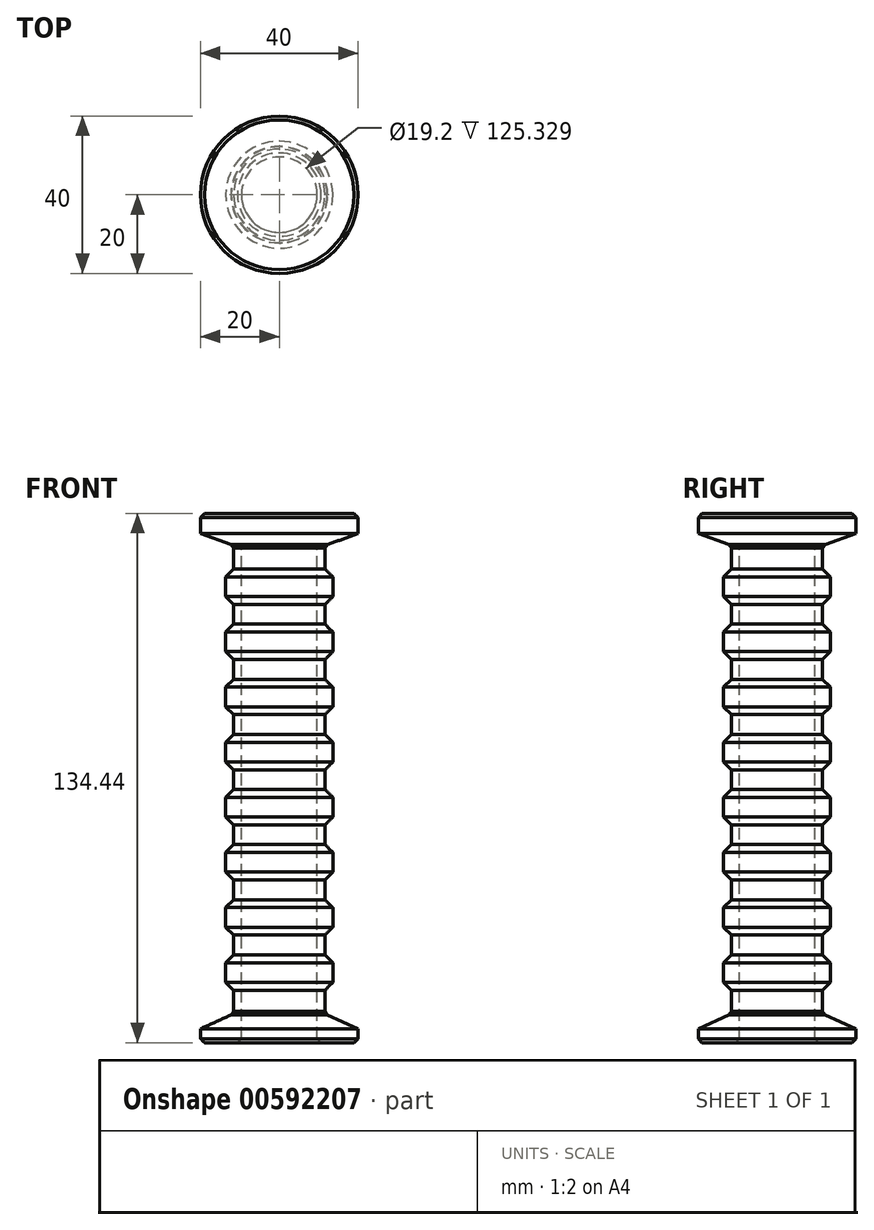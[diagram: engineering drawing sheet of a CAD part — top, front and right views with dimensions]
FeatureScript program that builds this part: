
annotation { "Feature Type Name" : "Feature", "Feature Type Description" : "" }
export const myFeature = defineFeature(function(context is Context, id is Id, definition is map)
    precondition{}
    {
        {
            var Q0;
            Q0=qCreatedBy(makeId("Front.planeOp"),FACE);
            var sketch = newSketch(context, id + "F0", { "sketchPlane" : qUnion([Q0])});
            skLineSegment(sketch, "E0", {"start": v(0, 89.56) * mm, "end": v(0, -84.94) * mm, "construction": true});
            skLineSegment(sketch, "E1", {"start": v(0, 55.8) * mm, "end": v(-20, 55.8) * mm});
            skLineSegment(sketch, "E2", {"start": v(-20, 55.8) * mm, "end": v(-20, 50.7) * mm});
            skLineSegment(sketch, "E3", {"start": v(-20, 50.7) * mm, "end": v(-11.6, 47.7) * mm});
            skLineSegment(sketch, "E4", {"start": v(-11.6, 47.7) * mm, "end": v(-11.6, 40.7) * mm, "construction": true});
            skLineSegment(sketch, "E5.bottom", {"start": v(-11.6, 40.7) * mm, "end": v(-13.6, 40.7) * mm});
            skLineSegment(sketch, "E5.top", {"start": v(-11.6, 33.7) * mm, "end": v(-13.6, 33.7) * mm});
            skLineSegment(sketch, "E5.right", {"start": v(-13.6, 40.7) * mm, "end": v(-13.6, 33.7) * mm});
            skLineSegment(sketch, "E6", {"start": v(-11.6, 47.7) * mm, "end": v(-11.6, 40.7) * mm});
            skLineSegment(sketch, "E7.0.1.0", {"start": v(-11.6, 33.7) * mm, "end": v(-11.6, 26.7) * mm});
            skLineSegment(sketch, "E7.0.1.1", {"start": v(-11.6, 26.7) * mm, "end": v(-13.6, 26.7) * mm});
            skLineSegment(sketch, "E7.0.1.2", {"start": v(-13.6, 26.7) * mm, "end": v(-13.6, 19.7) * mm});
            skLineSegment(sketch, "E7.0.1.3", {"start": v(-11.6, 19.7) * mm, "end": v(-13.6, 19.7) * mm});
            skLineSegment(sketch, "E7.0.2.0", {"start": v(-11.6, 19.7) * mm, "end": v(-11.6, 12.7) * mm});
            skLineSegment(sketch, "E7.0.2.1", {"start": v(-11.6, 12.7) * mm, "end": v(-13.6, 12.7) * mm});
            skLineSegment(sketch, "E7.0.2.2", {"start": v(-13.6, 12.7) * mm, "end": v(-13.6, 5.7) * mm});
            skLineSegment(sketch, "E7.0.2.3", {"start": v(-11.6, 5.7) * mm, "end": v(-13.6, 5.7) * mm});
            skLineSegment(sketch, "E7.0.3.0", {"start": v(-11.6, 5.7) * mm, "end": v(-11.6, -1.3) * mm});
            skLineSegment(sketch, "E7.0.3.1", {"start": v(-11.6, -1.3) * mm, "end": v(-13.6, -1.3) * mm});
            skLineSegment(sketch, "E7.0.3.2", {"start": v(-13.6, -1.3) * mm, "end": v(-13.6, -8.3) * mm});
            skLineSegment(sketch, "E7.0.3.3", {"start": v(-11.6, -8.3) * mm, "end": v(-13.6, -8.3) * mm});
            skLineSegment(sketch, "E7.0.4.0", {"start": v(-11.6, -8.3) * mm, "end": v(-11.6, -15.3) * mm});
            skLineSegment(sketch, "E7.0.4.1", {"start": v(-11.6, -15.3) * mm, "end": v(-13.6, -15.3) * mm});
            skLineSegment(sketch, "E7.0.4.2", {"start": v(-13.6, -15.3) * mm, "end": v(-13.6, -22.3) * mm});
            skLineSegment(sketch, "E7.0.4.3", {"start": v(-11.6, -22.3) * mm, "end": v(-13.6, -22.3) * mm});
            skLineSegment(sketch, "E7.0.5.0", {"start": v(-11.6, -22.3) * mm, "end": v(-11.6, -29.3) * mm});
            skLineSegment(sketch, "E7.0.5.1", {"start": v(-11.6, -29.3) * mm, "end": v(-13.6, -29.3) * mm});
            skLineSegment(sketch, "E7.0.5.2", {"start": v(-13.6, -29.3) * mm, "end": v(-13.6, -36.3) * mm});
            skLineSegment(sketch, "E7.0.5.3", {"start": v(-11.6, -36.3) * mm, "end": v(-13.6, -36.3) * mm});
            skLineSegment(sketch, "E7.0.6.0", {"start": v(-11.6, -36.3) * mm, "end": v(-11.6, -43.3) * mm});
            skLineSegment(sketch, "E7.0.6.1", {"start": v(-11.6, -43.3) * mm, "end": v(-13.6, -43.3) * mm});
            skLineSegment(sketch, "E7.0.6.2", {"start": v(-13.6, -43.3) * mm, "end": v(-13.6, -50.3) * mm});
            skLineSegment(sketch, "E7.0.6.3", {"start": v(-11.6, -50.3) * mm, "end": v(-13.6, -50.3) * mm});
            skLineSegment(sketch, "E7.0.7.0", {"start": v(-11.6, -50.3) * mm, "end": v(-11.6, -57.3) * mm});
            skLineSegment(sketch, "E7.0.7.1", {"start": v(-11.6, -57.3) * mm, "end": v(-13.6, -57.3) * mm});
            skLineSegment(sketch, "E7.0.7.2", {"start": v(-13.6, -57.3) * mm, "end": v(-13.6, -64.3) * mm});
            skLineSegment(sketch, "E7.0.7.3", {"start": v(-11.6, -64.3) * mm, "end": v(-13.6, -64.3) * mm});
            skLineSegment(sketch, "E7.direction1", {"start": v(-11.6, 40.7) * mm, "end": v(-9.6, 40.7) * mm, "construction": true});
            skLineSegment(sketch, "E7.direction2", {"start": v(-11.6, 33.7) * mm, "end": v(-11.6, 26.7) * mm, "construction": true});
            skLineSegment(sketch, "E8", {"start": v(-11.6, -64.3) * mm, "end": v(-11.6, -71.3) * mm});
            skLineSegment(sketch, "E9", {"start": v(-11.6, -71.3) * mm, "end": v(-20, -75.1) * mm});
            skLineSegment(sketch, "E10", {"start": v(-20, -75.1) * mm, "end": v(-20, -78.63) * mm});
            skLineSegment(sketch, "E11", {"start": v(-20, -78.63) * mm, "end": v(-9.6, -78.63) * mm});
            skLineSegment(sketch, "E12", {"start": v(-9.6, 47.7) * mm, "end": v(0, 47.7) * mm});
            skLineSegment(sketch, "E13", {"start": v(-9.6, 47.7) * mm, "end": v(-9.6, -78.63) * mm});
            skLineSegment(sketch, "E14.trimOffspring", {"start": v(-11.6, 33.7) * mm, "end": v(-11.6, -81.3) * mm, "construction": true});
            skLineSegment(sketch, "E15", {"start": v(0, 47.7) * mm, "end": v(0, 55.8) * mm});
            skSolve(sketch);
        }
        {
            var Q0;
            Q0 = qSketchRegion(id + "F0", true);
            var Q1;
            Q1=sQuery(id+"F0.wireOp",EDGE,"E0");
            revolve(context, id + "F1", {"entities" : qUnion([Q0]), "axis" : qUnion([Q1]), "revolveType" : RevolveType.FULL});
        }
        {
            var Q0;
            Q0=makeQuery(id+"F1.opRevolve","SWEPT_EDGE",EDGE,{"disambiguationData":[OSD([sQuery(id+"F0.wireOp",EDGE,"E5.bottom"),sQuery(id+"F0.wireOp",EDGE,"E5.right")])]});
            var Q1;
            Q1=makeQuery(id+"F1.opRevolve","SWEPT_EDGE",EDGE,{"disambiguationData":[OSD([sQuery(id+"F0.wireOp",EDGE,"E5.top"),sQuery(id+"F0.wireOp",EDGE,"E5.right")])]});
            var Q2;
            Q2=makeQuery(id+"F1.opRevolve","SWEPT_EDGE",EDGE,{"disambiguationData":[OSD([sQuery(id+"F0.wireOp",EDGE,"E7.0.1.1"),sQuery(id+"F0.wireOp",EDGE,"E7.0.1.2")])]});
            var Q3;
            Q3=makeQuery(id+"F1.opRevolve","SWEPT_EDGE",EDGE,{"disambiguationData":[OSD([sQuery(id+"F0.wireOp",EDGE,"E7.0.1.2"),sQuery(id+"F0.wireOp",EDGE,"E7.0.1.3")])]});
            var Q4;
            Q4=makeQuery(id+"F1.opRevolve","SWEPT_EDGE",EDGE,{"disambiguationData":[OSD([sQuery(id+"F0.wireOp",EDGE,"E7.0.2.1"),sQuery(id+"F0.wireOp",EDGE,"E7.0.2.2")])]});
            var Q5;
            Q5=makeQuery(id+"F1.opRevolve","SWEPT_EDGE",EDGE,{"disambiguationData":[OSD([sQuery(id+"F0.wireOp",EDGE,"E7.0.2.2"),sQuery(id+"F0.wireOp",EDGE,"E7.0.2.3")])]});
            var Q6;
            Q6=makeQuery(id+"F1.opRevolve","SWEPT_FACE",FACE,{"disambiguationData":[OSD([sQuery(id+"F0.wireOp",EDGE,"E7.0.3.2")])]});
            var Q7;
            Q7=makeQuery(id+"F1.opRevolve","SWEPT_FACE",FACE,{"disambiguationData":[OSD([sQuery(id+"F0.wireOp",EDGE,"E7.0.4.2")])]});
            var Q8;
            Q8=makeQuery(id+"F1.opRevolve","SWEPT_FACE",FACE,{"disambiguationData":[OSD([sQuery(id+"F0.wireOp",EDGE,"E7.0.5.2")])]});
            var Q9;
            Q9=makeQuery(id+"F1.opRevolve","SWEPT_FACE",FACE,{"disambiguationData":[OSD([sQuery(id+"F0.wireOp",EDGE,"E7.0.6.2")])]});
            var Q10;
            Q10=makeQuery(id+"F1.opRevolve","SWEPT_FACE",FACE,{"disambiguationData":[OSD([sQuery(id+"F0.wireOp",EDGE,"E7.0.7.2")])]});
            var Q11;
            Q11=makeQuery(id+"F1.opRevolve","SWEPT_FACE",FACE,{"disambiguationData":[OSD([sQuery(id+"F0.wireOp",EDGE,"E7.0.7.0")])]});
            var Q12;
            Q12=makeQuery(id+"F1.opRevolve","SWEPT_FACE",FACE,{"disambiguationData":[OSD([sQuery(id+"F0.wireOp",EDGE,"E7.0.6.0")])]});
            var Q13;
            Q13=makeQuery(id+"F1.opRevolve","SWEPT_FACE",FACE,{"disambiguationData":[OSD([sQuery(id+"F0.wireOp",EDGE,"E7.0.5.0")])]});
            var Q14;
            Q14=makeQuery(id+"F1.opRevolve","SWEPT_FACE",FACE,{"disambiguationData":[OSD([sQuery(id+"F0.wireOp",EDGE,"E7.0.4.0")])]});
            var Q15;
            Q15=makeQuery(id+"F1.opRevolve","SWEPT_FACE",FACE,{"disambiguationData":[OSD([sQuery(id+"F0.wireOp",EDGE,"E7.0.3.0")])]});
            var Q16;
            Q16=makeQuery(id+"F1.opRevolve","SWEPT_FACE",FACE,{"disambiguationData":[OSD([sQuery(id+"F0.wireOp",EDGE,"E7.0.2.0")])]});
            var Q17;
            Q17=makeQuery(id+"F1.opRevolve","SWEPT_FACE",FACE,{"disambiguationData":[OSD([sQuery(id+"F0.wireOp",EDGE,"E7.0.1.0")])]});
            var Q18;
            Q18=makeQuery(id+"F1.opRevolve","SWEPT_FACE",FACE,{"disambiguationData":[OSD([sQuery(id+"F0.wireOp",EDGE,"E6")])]});
            var Q19;
            Q19=makeQuery(id+"F1.opRevolve","SWEPT_FACE",FACE,{"disambiguationData":[OSD([sQuery(id+"F0.wireOp",EDGE,"E8")])]});
            var Q20;
            Q20=makeQuery(id+"F1.opRevolve","SWEPT_EDGE",EDGE,{"disambiguationData":[OSD([sQuery(id+"F0.wireOp",EDGE,"E11"),sQuery(id+"F0.wireOp",EDGE,"E13")])]});
            var Q21;
            Q21=makeQuery(id+"F1.opRevolve","SWEPT_EDGE",EDGE,{"disambiguationData":[OSD([sQuery(id+"F0.wireOp",EDGE,"E10"),sQuery(id+"F0.wireOp",EDGE,"E11")])]});
            var Q22;
            Q22=makeQuery(id+"F1.opRevolve","SWEPT_EDGE",EDGE,{"disambiguationData":[OSD([sQuery(id+"F0.wireOp",EDGE,"E1"),sQuery(id+"F0.wireOp",EDGE,"E2")])]});
            chamfer(context, id + "F2", {"entities" : qUnion([Q0, Q1, Q2, Q3, Q4, Q5, Q6, Q7, Q8, Q9, Q10, Q11, Q12, Q13, Q14, Q15, Q16, Q17, Q18, Q19, Q20, Q21, Q22]), "width" : 1 * mm, "tangentPropagation" : true});
        }
    });
